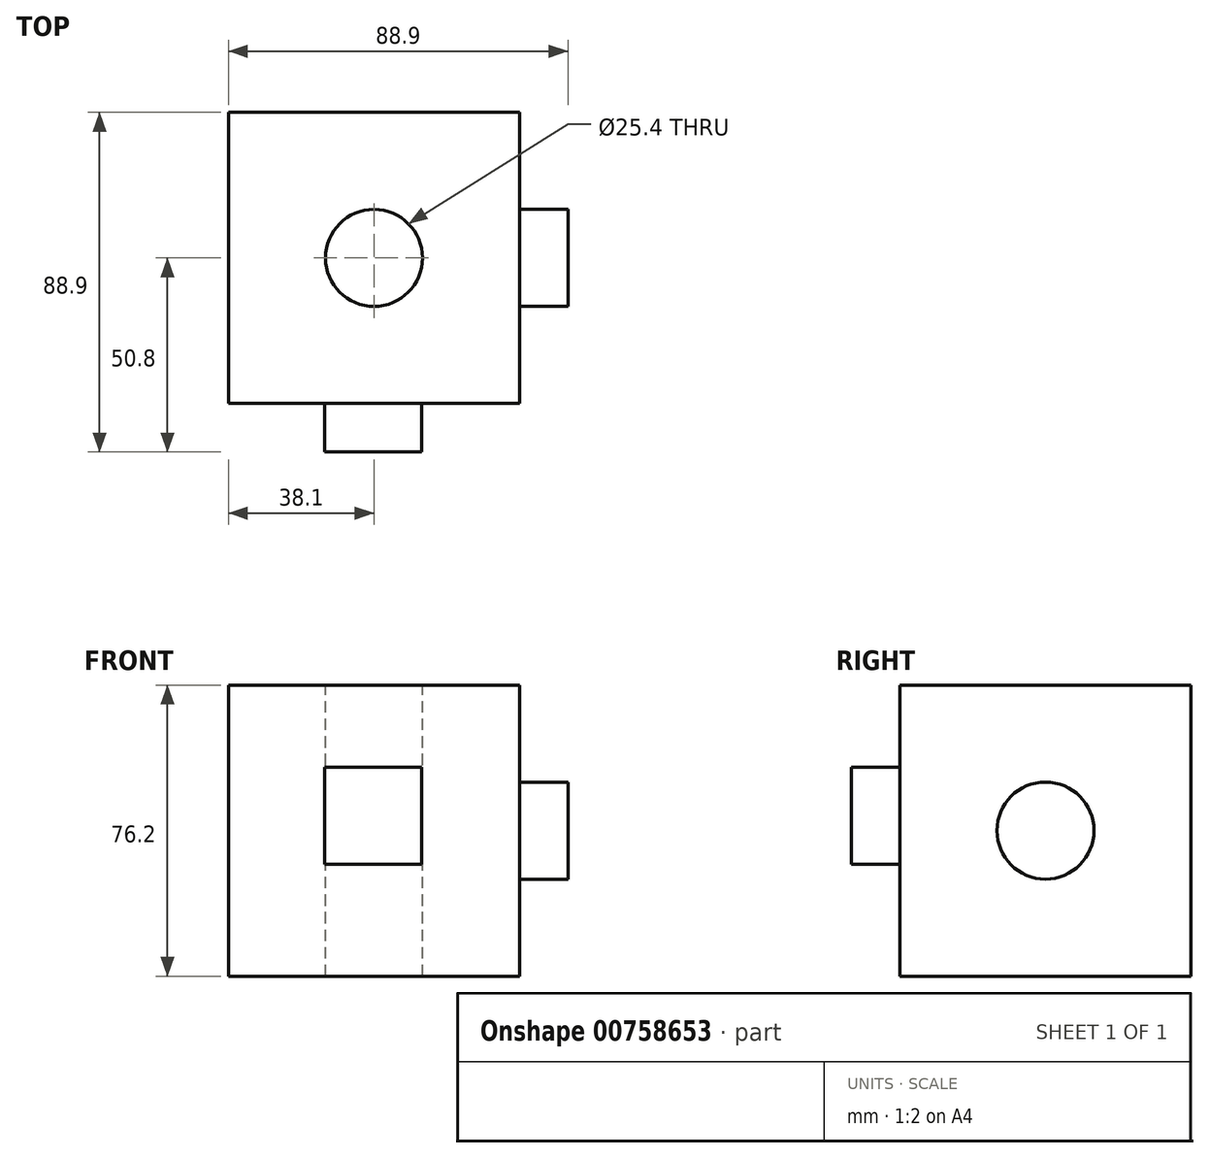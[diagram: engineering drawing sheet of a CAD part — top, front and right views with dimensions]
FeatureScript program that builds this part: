
annotation { "Feature Type Name" : "Feature", "Feature Type Description" : "" }
export const myFeature = defineFeature(function(context is Context, id is Id, definition is map)
    precondition{}
    {
        {
            var Q0;
            Q0=qCreatedBy(makeId("Front.planeOp"),FACE);
            var sketch = newSketch(context, id + "F0", { "sketchPlane" : qUnion([Q0])});
            skLineSegment(sketch, "E0.bottom", {"start": v(-76.2, 40.67) * mm, "end": v(0, 40.67) * mm});
            skLineSegment(sketch, "E0.top", {"start": v(-76.2, -35.53) * mm, "end": v(0, -35.53) * mm});
            skLineSegment(sketch, "E0.left", {"start": v(-76.2, 40.67) * mm, "end": v(-76.2, -35.53) * mm});
            skLineSegment(sketch, "E0.right", {"start": v(0, 40.67) * mm, "end": v(0, -35.53) * mm});
            skSolve(sketch);
        }
        {
            var Q0;
            Q0=makeQuery(id+"F0.imprint","IMPRINT",FACE,{"disambiguationData":[TD([[makeQuery(id+"F0.imprint","IMPRINT",EDGE,{"derivedFrom":sQuery(id+"F0.wireOp",EDGE,"E0.bottom")}),-1.0]])]});
            extrude(context, id + "F1", {"entities" : qUnion([Q0]), "depth" : 76.2 * mm, "offsetDistance" : 25.4 * mm});
        }
        {
            var Q0;
            Q0=makeQuery(id+"F1.opExtrude","CAP_FACE",FACE,{"disambiguationData":[OSD([sQuery(id+"F0.wireOp",EDGE,"E0.bottom"),sQuery(id+"F0.wireOp",EDGE,"E0.top"),sQuery(id+"F0.wireOp",EDGE,"E0.left"),sQuery(id+"F0.wireOp",EDGE,"E0.right")])],"isStart":false});
            var sketch = newSketch(context, id + "F2", { "sketchPlane" : qUnion([Q0])});
            skLineSegment(sketch, "E1.bottom", {"start": v(-51.08, 19.19) * mm, "end": v(-25.68, 19.19) * mm});
            skLineSegment(sketch, "E1.top", {"start": v(-51.08, -6.21) * mm, "end": v(-25.68, -6.21) * mm});
            skLineSegment(sketch, "E1.left", {"start": v(-51.08, 19.19) * mm, "end": v(-51.08, -6.21) * mm});
            skLineSegment(sketch, "E1.right", {"start": v(-25.68, 19.19) * mm, "end": v(-25.68, -6.21) * mm});
            skSolve(sketch);
        }
        {
            var Q0;
            Q0=makeQuery(id+"F2.imprint","IMPRINT",FACE,{"disambiguationData":[TD([[makeQuery(id+"F2.imprint","IMPRINT",EDGE,{"derivedFrom":sQuery(id+"F2.wireOp",EDGE,"E1.bottom")}),-1.0]])]});
            extrude(context, id + "F3", {"entities" : qUnion([Q0]), "operationType" : NewBodyOperationType.ADD, "depth" : 12.7 * mm, "offsetDistance" : 25.4 * mm});
        }
        {
            var Q0;
            Q0=makeQuery(id+"F1.opExtrude","SWEPT_FACE",FACE,{"disambiguationData":[OSD([sQuery(id+"F0.wireOp",EDGE,"E0.right")])]});
            var sketch = newSketch(context, id + "F4", { "sketchPlane" : qUnion([Q0])});
            skCircle(sketch, "E2", {"center": v(-38.1, 2.57) * mm, "radius": 12.7 * mm});
            skSolve(sketch);
        }
        {
            var Q0;
            Q0=makeQuery(id+"F1.opExtrude","SWEPT_FACE",FACE,{"disambiguationData":[OSD([sQuery(id+"F0.wireOp",EDGE,"E0.bottom")])]});
            var sketch = newSketch(context, id + "F5", { "sketchPlane" : qUnion([Q0])});
            skPoint(sketch, "E3", {"position": v(-38.1, -38.1) * mm});
            skSolve(sketch);
        }
        {
            var Q0;
            Q0=sQuery(id+"F5.wireOp",VERTEX,"E3");
            var Q1;
            Q1=makeQuery(id+"F1.opExtrude","SWEPT_BODY",BODY,{"disambiguationData":[OSD([sQuery(id+"F0.wireOp",EDGE,"E0.bottom"),sQuery(id+"F0.wireOp",EDGE,"E0.top"),sQuery(id+"F0.wireOp",EDGE,"E0.left"),sQuery(id+"F0.wireOp",EDGE,"E0.right")])]});
            hole(context, id + "F6", {"style" : HoleStyle.SIMPLE, "endStyle" : HoleEndStyle.THROUGH, "holeDiameter" : 25.4 * mm, "majorDiameter" : 9.52 * mm, "isTappedThrough" : true, "tappedDepth" : 12.71 * mm, "tapClearance" : 3, "locations" : qUnion([Q0]), "scope" : qUnion([Q1])});
        }
        {
            var Q0;
            Q0 = qSketchRegion(id + "F4", true);
            extrude(context, id + "F7", {"entities" : qUnion([Q0]), "operationType" : NewBodyOperationType.ADD, "depth" : 12.7 * mm, "offsetDistance" : 25.4 * mm});
        }
    });
